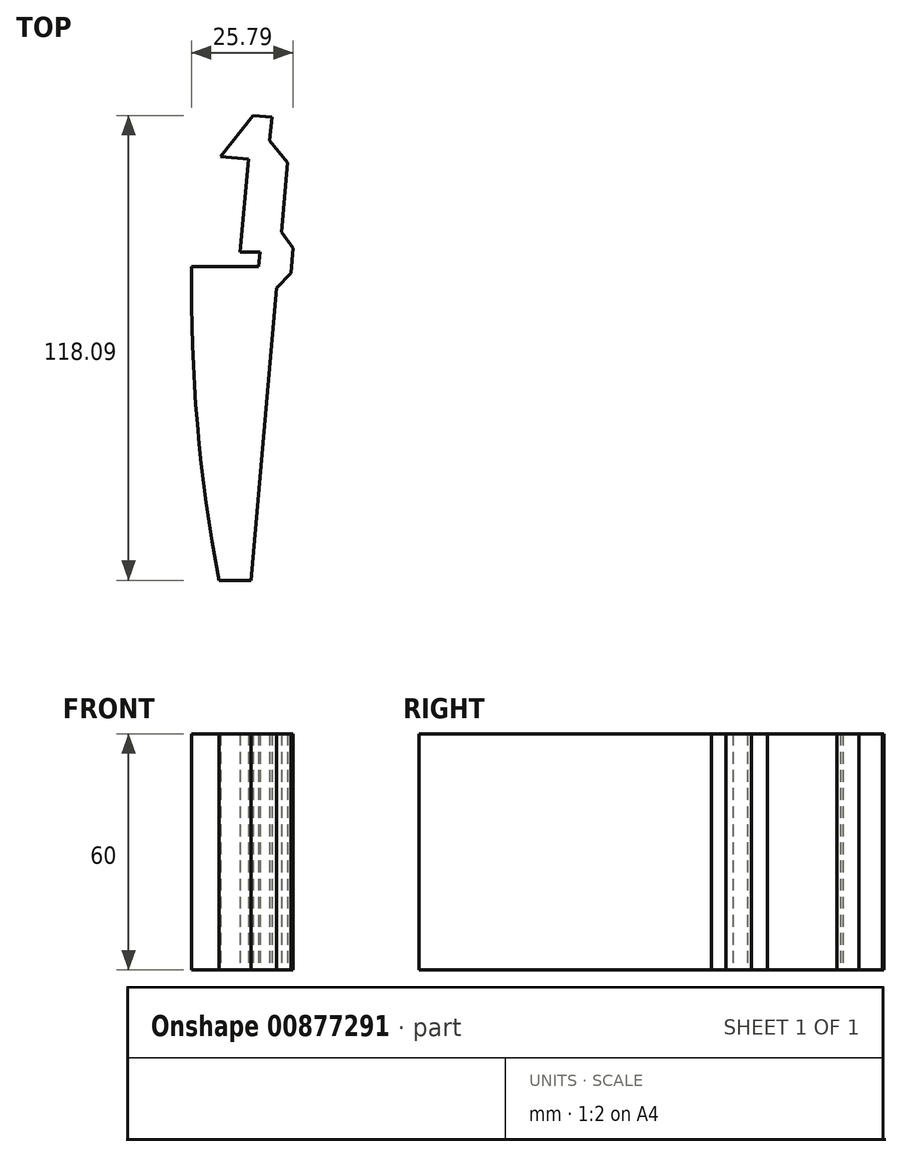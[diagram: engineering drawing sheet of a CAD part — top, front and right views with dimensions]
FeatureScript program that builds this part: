
annotation { "Feature Type Name" : "Feature", "Feature Type Description" : "" }
export const myFeature = defineFeature(function(context is Context, id is Id, definition is map)
    precondition{}
    {
        {
            var Q0;
            Q0=qCreatedBy(makeId("Top.planeOp"),FACE);
            var sketch = newSketch(context, id + "F0", { "sketchPlane" : qUnion([Q0])});
            skLineSegment(sketch, "E0", {"start": v(-52.15, 19.48) * mm, "end": v(-35.15, 19.48) * mm});
            skLineSegment(sketch, "E1", {"start": v(-35.15, 19.48) * mm, "end": v(-34.82, 23.23) * mm});
            skLineSegment(sketch, "E2.0", {"start": v(-30.19, 18.81) * mm, "end": v(-27.82, 45.94) * mm});
            skLineSegment(sketch, "E3", {"start": v(-52.15, 19.48) * mm, "end": v(-45.18, -60.22) * mm});
            skLineSegment(sketch, "E4", {"start": v(-45.18, -60.22) * mm, "end": v(-37.1, -60.22) * mm});
            skLineSegment(sketch, "E5", {"start": v(-30.19, 18.81) * mm, "end": v(-37.1, -60.22) * mm});
            skLineSegment(sketch, "E6", {"start": v(-34.82, 23.23) * mm, "end": v(-39.84, 23.23) * mm});
            skLineSegment(sketch, "E7", {"start": v(-39.84, 23.23) * mm, "end": v(-37.78, 46.8) * mm});
            skLineSegment(sketch, "E8", {"start": v(-37.78, 46.8) * mm, "end": v(-44.78, 47.42) * mm});
            skLineSegment(sketch, "E9", {"start": v(-36.62, 57.87) * mm, "end": v(-44.78, 47.42) * mm});
            skLineSegment(sketch, "E10", {"start": v(-37.78, 46.8) * mm, "end": v(-27.82, 45.94) * mm});
            skLineSegment(sketch, "E11", {"start": v(-34.82, 23.23) * mm, "end": v(-31.83, 57.45) * mm});
            skLineSegment(sketch, "E12", {"start": v(-36.62, 57.87) * mm, "end": v(-31.83, 57.45) * mm});
            skLineSegment(sketch, "E13", {"start": v(-27.82, 45.94) * mm, "end": v(-32.35, 51.5) * mm});
            skArc(sketch, "E14", {"start": v(-52.15, 19.48) * mm, "mid": v(-50.75, -20.55) * mm, "end": v(-45.18, -60.22) * mm});
            skLineSegment(sketch, "E15", {"start": v(-30.61, 14) * mm, "end": v(-26.99, 17.78) * mm});
            skLineSegment(sketch, "E16", {"start": v(-26.99, 17.78) * mm, "end": v(-26.42, 24.25) * mm});
            skLineSegment(sketch, "E17", {"start": v(-26.42, 24.25) * mm, "end": v(-29.36, 28.3) * mm});
            skSolve(sketch);
        }
        {
            var Q0;
            {var subQ1=sQuery(id+"F0.wireOp",EDGE,"E8");Q0=makeQuery(id+"F0.imprint","IMPRINT",FACE,{"disambiguationData":[TD([[makeQuery(id+"F0.imprint","IMPRINT",EDGE,{"derivedFrom":subQ1}),-1.0]])]});}
            var Q1;
            {var subQ0=sQuery(id+"F0.wireOp",EDGE,"E13");Q1=makeQuery(id+"F0.imprint","IMPRINT",FACE,{"disambiguationData":[TD([[makeQuery(id+"F0.imprint","IMPRINT",EDGE,{"derivedFrom":subQ0}),1.0]])]});}
            var Q2;
            {var subQ0=sQuery(id+"F0.wireOp",EDGE,"E6");Q2=makeQuery(id+"F0.imprint","IMPRINT",FACE,{"disambiguationData":[TD([[makeQuery(id+"F0.imprint","IMPRINT",EDGE,{"derivedFrom":subQ0}),-1.0]])]});}
            var Q3;
            Q3=makeQuery(id+"F0.imprint","IMPRINT",FACE,{"disambiguationData":[TD([[makeQuery(id+"F0.imprint","IMPRINT",EDGE,{"derivedFrom":sQuery(id+"F0.wireOp",EDGE,"E0")}),-1.0]])]});
            var Q4;
            {var subQ0=sQuery(id+"F0.wireOp",EDGE,"E15");Q4=makeQuery(id+"F0.imprint","IMPRINT",FACE,{"disambiguationData":[TD([[makeQuery(id+"F0.imprint","IMPRINT",EDGE,{"derivedFrom":subQ0}),1.0]])]});}
            var Q5;
            Q5=makeQuery(id+"F0.imprint","IMPRINT",FACE,{"disambiguationData":[TD([[makeQuery(id+"F0.imprint","IMPRINT",EDGE,{"derivedFrom":sQuery(id+"F0.wireOp",EDGE,"E3")}),-1.0]])]});
            extrude(context, id + "F1", {"entities" : qUnion([Q0, Q1, Q2, Q3, Q4, Q5]), "depth" : 60 * mm, "offsetDistance" : 25 * mm});
        }
    });
